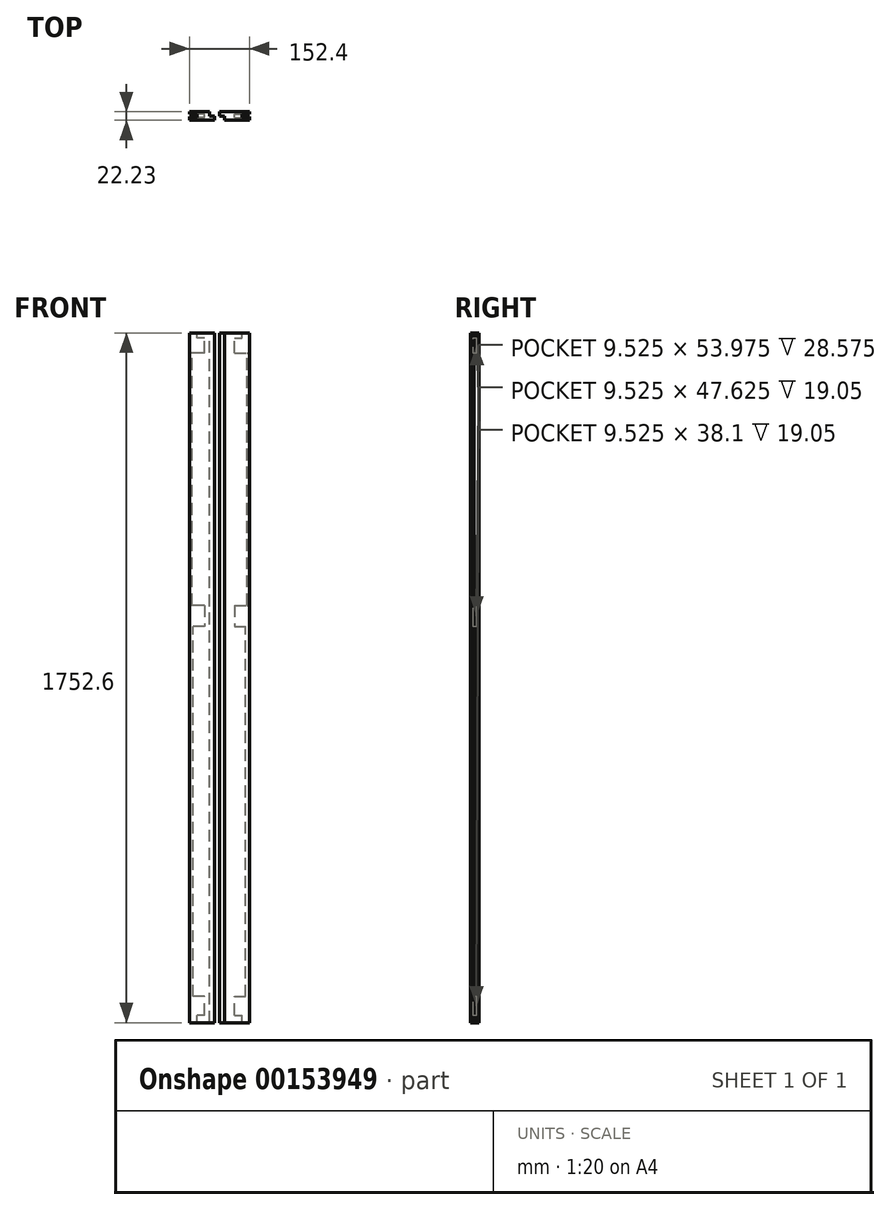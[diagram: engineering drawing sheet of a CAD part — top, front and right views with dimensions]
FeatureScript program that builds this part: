
annotation { "Feature Type Name" : "Feature", "Feature Type Description" : "" }
export const myFeature = defineFeature(function(context is Context, id is Id, definition is map)
    precondition{}
    {
        {
            var Q0;
            Q0=qCreatedBy(makeId("Front.planeOp"),FACE);
            var sketch = newSketch(context, id + "F0", { "sketchPlane" : qUnion([Q0])});
            skLineSegment(sketch, "E0.bottom", {"start": v(0, 0) * mm, "end": v(-76.2, 0) * mm});
            skLineSegment(sketch, "E0.top", {"start": v(0, 1778) * mm, "end": v(-76.2, 1778) * mm});
            skLineSegment(sketch, "E0.left", {"start": v(0, 0) * mm, "end": v(0, 1778) * mm});
            skLineSegment(sketch, "E0.right", {"start": v(-76.2, 0) * mm, "end": v(-76.2, 1778) * mm});
            skSolve(sketch);
        }
        {
            var Q0;
            Q0=makeQuery(id+"F0.imprint","IMPRINT",FACE,{"disambiguationData":[TD([[makeQuery(id+"F0.imprint","IMPRINT",EDGE,{"derivedFrom":sQuery(id+"F0.wireOp",EDGE,"E0.bottom")}),-1.0]])]});
            extrude(context, id + "F1", {"entities" : qUnion([Q0]), "depth" : 22.22 * mm});
        }
        {
            var Q0;
            Q0=makeQuery(id+"F1.opExtrude","SWEPT_FACE",FACE,{"disambiguationData":[OSD([sQuery(id+"F0.wireOp",EDGE,"E0.right")])]});
            var sketch = newSketch(context, id + "F2", { "sketchPlane" : qUnion([Q0])});
            skLineSegment(sketch, "E1.bottom", {"start": v(6.35, 0) * mm, "end": v(15.88, 0) * mm});
            skLineSegment(sketch, "E1.top", {"start": v(6.35, 79.38) * mm, "end": v(15.88, 79.38) * mm});
            skLineSegment(sketch, "E1.left", {"start": v(6.35, 0) * mm, "end": v(6.35, 79.37) * mm});
            skLineSegment(sketch, "E1.right", {"start": v(15.88, 0) * mm, "end": v(15.88, 79.37) * mm});
            skLineSegment(sketch, "E2.bottom", {"start": v(15.87, 1714.5) * mm, "end": v(6.35, 1714.5) * mm});
            skLineSegment(sketch, "E2.top", {"start": v(15.87, 1778) * mm, "end": v(6.35, 1778) * mm});
            skLineSegment(sketch, "E2.left", {"start": v(15.87, 1714.5) * mm, "end": v(15.87, 1778) * mm});
            skLineSegment(sketch, "E2.right", {"start": v(6.35, 1714.5) * mm, "end": v(6.35, 1778) * mm});
            skLineSegment(sketch, "E3", {"start": v(6.35, 31.75) * mm, "end": v(15.88, 31.75) * mm});
            skLineSegment(sketch, "E4", {"start": v(6.35, 1752.6) * mm, "end": v(15.87, 1752.6) * mm});
            skLineSegment(sketch, "E5.bottom", {"start": v(15.88, 1073.15) * mm, "end": v(6.35, 1073.15) * mm});
            skLineSegment(sketch, "E5.top", {"start": v(15.87, 1019.18) * mm, "end": v(6.35, 1019.18) * mm});
            skLineSegment(sketch, "E5.left", {"start": v(15.87, 1073.15) * mm, "end": v(15.87, 1019.18) * mm});
            skLineSegment(sketch, "E5.right", {"start": v(6.35, 1073.15) * mm, "end": v(6.35, 1019.18) * mm});
            skLineSegment(sketch, "E6.bottom", {"start": v(0, 1098.55) * mm, "end": v(22.22, 1098.55) * mm, "construction": true});
            skLineSegment(sketch, "E6.top", {"start": v(0, 993.78) * mm, "end": v(22.23, 993.78) * mm, "construction": true});
            skLineSegment(sketch, "E6.left", {"start": v(0, 993.78) * mm, "end": v(0, 1098.55) * mm, "construction": true});
            skLineSegment(sketch, "E6.right", {"start": v(22.22, 993.78) * mm, "end": v(22.22, 1098.55) * mm, "construction": true});
            skSolve(sketch);
        }
        {
            var Q0;
            {var subQ0=sQuery(id+"F2.wireOp",EDGE,"E2.bottom");Q0=makeQuery(id+"F2.imprint","IMPRINT",FACE,{"disambiguationData":[TD([[makeQuery(id+"F2.imprint","IMPRINT",EDGE,{"derivedFrom":subQ0}),-1.0]])]});}
            var Q1;
            {var subQ0=sQuery(id+"F2.wireOp",EDGE,"E1.top");Q1=makeQuery(id+"F2.imprint","IMPRINT",FACE,{"disambiguationData":[TD([[makeQuery(id+"F2.imprint","IMPRINT",EDGE,{"derivedFrom":subQ0}),-1.0]])]});}
            var Q2;
            Q2=makeQuery(id+"F2.imprint","IMPRINT",FACE,{"disambiguationData":[TD([[makeQuery(id+"F2.imprint","IMPRINT",EDGE,{"derivedFrom":sQuery(id+"F2.wireOp",EDGE,"E5.bottom")}),1.0]])]});
            extrude(context, id + "F3", {"entities" : qUnion([Q0, Q1, Q2]), "operationType" : NewBodyOperationType.REMOVE, "oppositeDirection" : true, "depth" : 38.1 * mm});
        }
        {
            var Q0;
            {var subQ0=sQuery(id+"F2.wireOp",EDGE,"E2.top");Q0=makeQuery(id+"F2.imprint","IMPRINT",FACE,{"disambiguationData":[TD([[makeQuery(id+"F2.imprint","IMPRINT",EDGE,{"derivedFrom":subQ0}),1.0]])]});}
            var Q1;
            {var subQ0=sQuery(id+"F2.wireOp",EDGE,"E1.bottom");Q1=makeQuery(id+"F2.imprint","IMPRINT",FACE,{"disambiguationData":[TD([[makeQuery(id+"F2.imprint","IMPRINT",EDGE,{"derivedFrom":subQ0}),-1.0]])]});}
            extrude(context, id + "F4", {"entities" : qUnion([Q0, Q1]), "operationType" : NewBodyOperationType.REMOVE, "oppositeDirection" : true, "depth" : 19.05 * mm});
        }
        {
            var Q0;
            Q0=makeQuery(id+"F1.opExtrude","CAP_FACE",FACE,{"disambiguationData":[OSD([sQuery(id+"F0.wireOp",EDGE,"E0.bottom"),sQuery(id+"F0.wireOp",EDGE,"E0.top"),sQuery(id+"F0.wireOp",EDGE,"E0.left"),sQuery(id+"F0.wireOp",EDGE,"E0.right")])],"isStart":false});
            var sketch = newSketch(context, id + "F5", { "sketchPlane" : qUnion([Q0])});
            skLineSegment(sketch, "E7", {"start": v(-76.2, 12.7) * mm, "end": v(0, 12.7) * mm});
            skLineSegment(sketch, "E8", {"start": v(-76.2, 1765.3) * mm, "end": v(0, 1765.3) * mm});
            skSolve(sketch);
        }
        {
            var Q0;
            Q0 = qSketchRegion(id + "F5", true);
            var Q1;
            {var subQ0=sQuery(id+"F5.wireOp",EDGE,"E8");Q1=makeQuery(id+"F5.imprint","IMPRINT",FACE,{"disambiguationData":[TD([[makeQuery(id+"F5.imprint","IMPRINT",EDGE,{"derivedFrom":subQ0}),1.0]])]});}
            var Q2;
            {var subQ0=sQuery(id+"F5.wireOp",EDGE,"E7");Q2=makeQuery(id+"F5.imprint","IMPRINT",FACE,{"disambiguationData":[TD([[makeQuery(id+"F5.imprint","IMPRINT",EDGE,{"derivedFrom":subQ0}),-1.0]])]});}
            extrude(context, id + "F6", {"entities" : qUnion([Q0, Q1, Q2]), "operationType" : NewBodyOperationType.REMOVE, "endBound" : BoundingType.THROUGH_ALL, "oppositeDirection" : true, "depth" : 25.4 * mm});
        }
        {
            var Q0;
            Q0=makeQuery(id+"F1.opExtrude","SWEPT_FACE",FACE,{"disambiguationData":[OSD([sQuery(id+"F0.wireOp",EDGE,"E0.right")])]});
            var sketch = newSketch(context, id + "F7", { "sketchPlane" : qUnion([Q0])});
            skLineSegment(sketch, "E9.bottom", {"start": v(15.88, 79.37) * mm, "end": v(6.35, 79.37) * mm});
            skLineSegment(sketch, "E9.top", {"start": v(15.87, 1019.18) * mm, "end": v(6.35, 1019.18) * mm});
            skLineSegment(sketch, "E9.left", {"start": v(15.88, 79.37) * mm, "end": v(15.87, 1019.18) * mm});
            skLineSegment(sketch, "E9.right", {"start": v(6.35, 79.37) * mm, "end": v(6.35, 1019.18) * mm});
            skSolve(sketch);
        }
        {
            var Q0;
            {var subQ0=sQuery(id+"F7.wireOp",EDGE,"E9.top");Q0=makeQuery(id+"F7.imprint","IMPRINT",FACE,{"disambiguationData":[TD([[makeQuery(id+"F7.imprint","IMPRINT",EDGE,{"derivedFrom":subQ0}),1.0]])]});}
            var Q1;
            {var subQ0=sQuery(id+"F7.wireOp",EDGE,"E9.bottom");Q1=makeQuery(id+"F7.imprint","IMPRINT",FACE,{"disambiguationData":[TD([[makeQuery(id+"F7.imprint","IMPRINT",EDGE,{"derivedFrom":subQ0}),1.0]])]});}
            extrude(context, id + "F8", {"entities" : qUnion([Q0, Q1]), "operationType" : NewBodyOperationType.REMOVE, "oppositeDirection" : true, "depth" : 9.52 * mm});
        }
        {
            var Q0;
            Q0=makeQuery(id+"F1.opExtrude","SWEPT_FACE",FACE,{"disambiguationData":[OSD([sQuery(id+"F0.wireOp",EDGE,"E0.right")])]});
            var sketch = newSketch(context, id + "F9", { "sketchPlane" : qUnion([Q0])});
            skLineSegment(sketch, "E10.bottom", {"start": v(0, 1714.5) * mm, "end": v(12.7, 1714.5) * mm});
            skLineSegment(sketch, "E10.top", {"start": v(0, 1073.15) * mm, "end": v(12.7, 1073.15) * mm});
            skLineSegment(sketch, "E10.left", {"start": v(0, 1714.5) * mm, "end": v(0, 1073.15) * mm});
            skLineSegment(sketch, "E10.right", {"start": v(12.7, 1714.5) * mm, "end": v(12.7, 1073.15) * mm});
            skSolve(sketch);
        }
        {
            var Q0;
            {var subQ5=sQuery(id+"F9.wireOp",EDGE,"E10.left");Q0=makeQuery(id+"F9.imprint","IMPRINT",FACE,{"disambiguationData":[TD([[makeQuery(id+"F9.imprint","IMPRINT",EDGE,{"derivedFrom":subQ5}),-1.0]])]});}
            extrude(context, id + "F10", {"entities" : qUnion([Q0]), "operationType" : NewBodyOperationType.REMOVE, "oppositeDirection" : true, "depth" : 6.35 * mm});
        }
        {
            var Q0;
            Q0=makeQuery(id+"F1.opExtrude","SWEPT_BODY",BODY,{"disambiguationData":[OSD([sQuery(id+"F0.wireOp",EDGE,"E0.bottom"),sQuery(id+"F0.wireOp",EDGE,"E0.top"),sQuery(id+"F0.wireOp",EDGE,"E0.left"),sQuery(id+"F0.wireOp",EDGE,"E0.right")])]});
            var Q1;
            Q1=qCreatedBy(makeId("Right.planeOp"),FACE);
            mirror(context, id + "F11", {"entities" : qUnion([Q0]), "mirrorPlane" : qUnion([Q1])});
        }
        {
            var Q0;
            Q0=makeQuery(id+"F6.boolean.opBoolean","COPY",FACE,{"derivedFrom":makeQuery(id+"F6.opExtrude","SWEPT_FACE",FACE,{"disambiguationData":[OSD([sQuery(id+"F5.wireOp",EDGE,"E8")])]})});
            var sketch = newSketch(context, id + "F12", { "sketchPlane" : qUnion([Q0])});
            skLineSegment(sketch, "E11.bottom", {"start": v(-25.4, 0) * mm, "end": v(0, 0) * mm});
            skLineSegment(sketch, "E11.top", {"start": v(-25.4, -11.11) * mm, "end": v(0, -11.11) * mm});
            skLineSegment(sketch, "E11.left", {"start": v(-25.4, 0) * mm, "end": v(-25.4, -11.11) * mm});
            skLineSegment(sketch, "E11.right", {"start": v(0, 0) * mm, "end": v(0, -11.11) * mm});
            skLineSegment(sketch, "E12", {"start": v(-12.7, -11.11) * mm, "end": v(-12.7, -22.23) * mm});
            skSolve(sketch);
        }
        {
            var Q0;
            Q0=makeQuery(id+"F12.imprint","IMPRINT",FACE,{"disambiguationData":[TD([[makeQuery(id+"F12.imprint","IMPRINT",EDGE,{"derivedFrom":sQuery(id+"F12.wireOp",EDGE,"E11.bottom")}),-1.0]])]});
            var Q1;
            {var subQ4=sQuery(id+"F12.wireOp",EDGE,"E12");Q1=makeQuery(id+"F12.imprint","IMPRINT",FACE,{"disambiguationData":[TD([[makeQuery(id+"F12.imprint","IMPRINT",EDGE,{"derivedFrom":subQ4}),1.0]])]});}
            extrude(context, id + "F13", {"entities" : qUnion([Q0, Q1]), "operationType" : NewBodyOperationType.REMOVE, "endBound" : BoundingType.UP_TO_NEXT, "oppositeDirection" : true, "depth" : 25.4 * mm});
        }
        {
            var Q0;
            Q0=makeQuery(id+"F11.opPattern","COPY",FACE,{"derivedFrom":makeQuery(id+"F6.boolean.opBoolean","COPY",FACE,{"derivedFrom":makeQuery(id+"F6.opExtrude","SWEPT_FACE",FACE,{"disambiguationData":[OSD([sQuery(id+"F5.wireOp",EDGE,"E8")])]})}),"instanceName":"1"});
            var sketch = newSketch(context, id + "F14", { "sketchPlane" : qUnion([Q0])});
            skLineSegment(sketch, "E13.bottom", {"start": v(0, -22.23) * mm, "end": v(12.7, -22.23) * mm});
            skLineSegment(sketch, "E13.top", {"start": v(0, -11.11) * mm, "end": v(12.7, -11.11) * mm});
            skLineSegment(sketch, "E13.left", {"start": v(0, -22.23) * mm, "end": v(0, -11.11) * mm});
            skLineSegment(sketch, "E13.right", {"start": v(12.7, -22.23) * mm, "end": v(12.7, -11.11) * mm});
            skSolve(sketch);
        }
        {
            var Q0;
            Q0=makeQuery(id+"F14.imprint","IMPRINT",FACE,{"disambiguationData":[TD([[makeQuery(id+"F14.imprint","IMPRINT",EDGE,{"derivedFrom":sQuery(id+"F14.wireOp",EDGE,"E13.bottom")}),-1.0]])]});
            extrude(context, id + "F15", {"entities" : qUnion([Q0]), "operationType" : NewBodyOperationType.REMOVE, "endBound" : BoundingType.UP_TO_NEXT, "oppositeDirection" : true, "depth" : 25.4 * mm});
        }
    });
